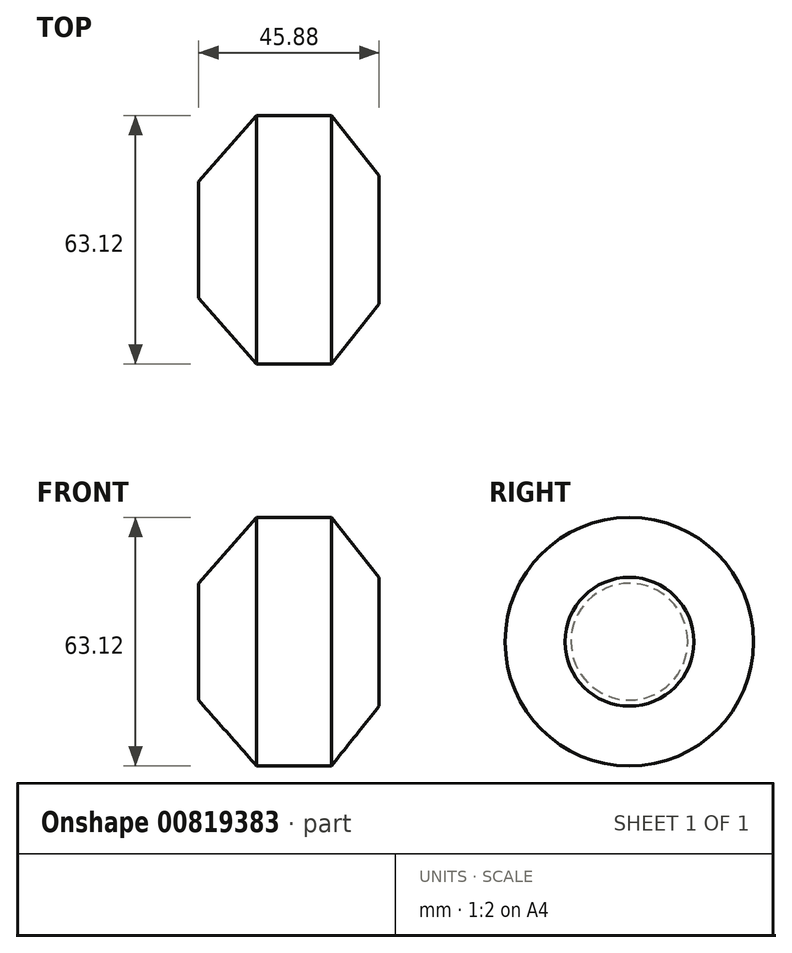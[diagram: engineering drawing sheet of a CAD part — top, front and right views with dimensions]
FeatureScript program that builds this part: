
annotation { "Feature Type Name" : "Feature", "Feature Type Description" : "" }
export const myFeature = defineFeature(function(context is Context, id is Id, definition is map)
    precondition{}
    {
        {
            var Q0;
            Q0=qCreatedBy(makeId("Front.planeOp"),FACE);
            var sketch = newSketch(context, id + "F0", { "sketchPlane" : qUnion([Q0])});
            skLineSegment(sketch, "E0", {"start": v(12.86, 0) * mm, "end": v(12.86, 14.84) * mm});
            skLineSegment(sketch, "E1", {"start": v(12.86, 14.84) * mm, "end": v(27.56, 31.56) * mm});
            skLineSegment(sketch, "E2", {"start": v(27.56, 31.56) * mm, "end": v(46.57, 31.56) * mm});
            skLineSegment(sketch, "E3", {"start": v(46.57, 31.56) * mm, "end": v(58.74, 16.36) * mm});
            skLineSegment(sketch, "E4", {"start": v(58.74, 16.36) * mm, "end": v(58.74, 0) * mm});
            skLineSegment(sketch, "E5", {"start": v(58.74, 0) * mm, "end": v(12.86, 0) * mm});
            skSolve(sketch);
        }
        {
            var Q0;
            Q0=makeQuery(id+"F0.imprint","IMPRINT",FACE,{"disambiguationData":[TD([[makeQuery(id+"F0.imprint","IMPRINT",EDGE,{"derivedFrom":sQuery(id+"F0.wireOp",EDGE,"E0")}),-1.0]])]});
            var Q1;
            Q1=sQuery(id+"F0.wireOp",EDGE,"E5");
            revolve(context, id + "F1", {"surfaceOperationType" : NewSurfaceOperationType.NEW, "entities" : qUnion([Q0]), "axis" : qUnion([Q1]), "revolveType" : RevolveType.FULL});
        }
    });
